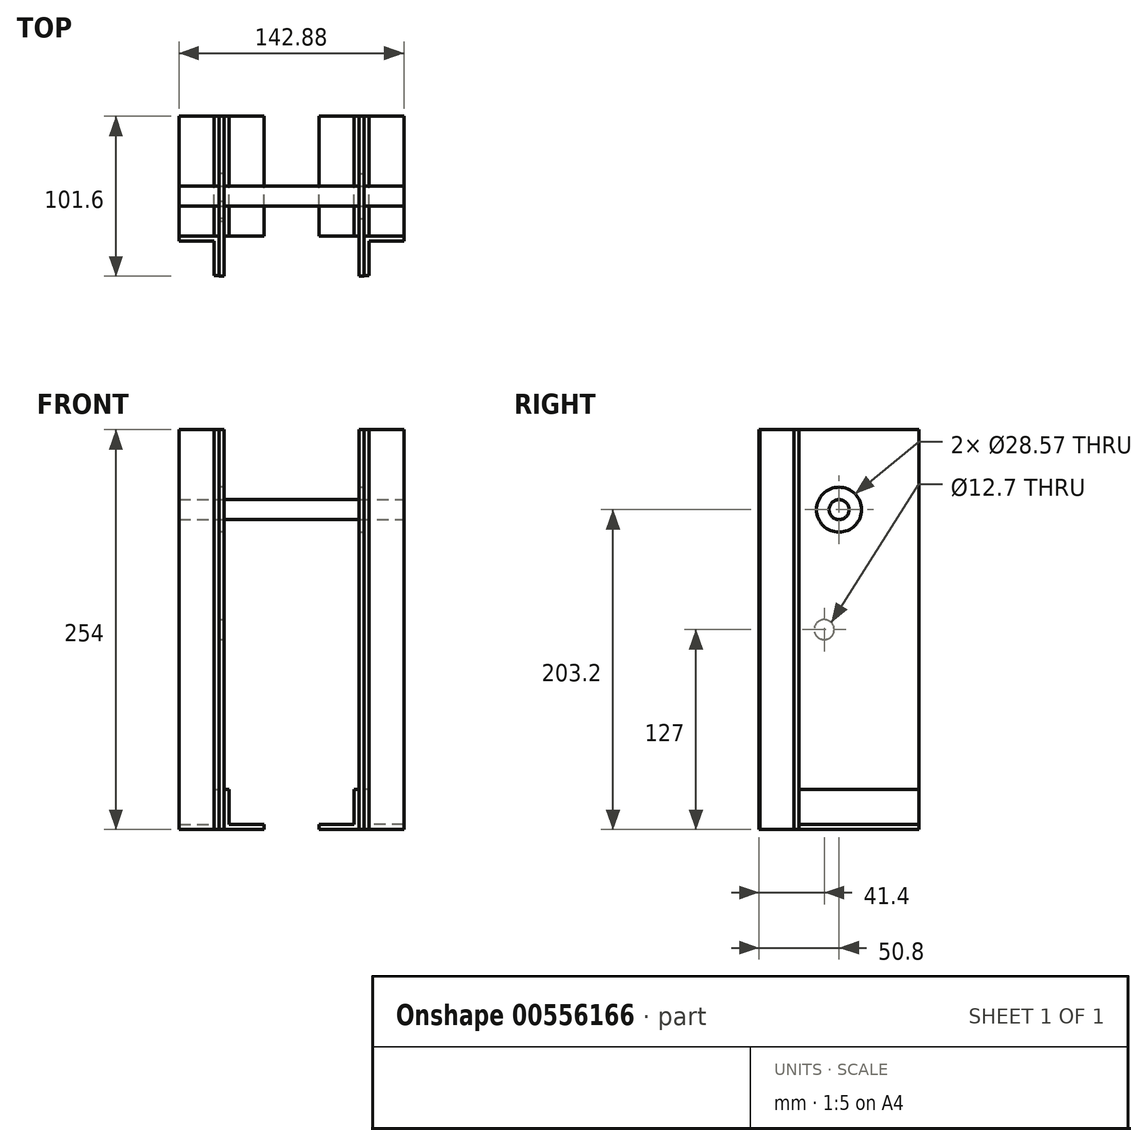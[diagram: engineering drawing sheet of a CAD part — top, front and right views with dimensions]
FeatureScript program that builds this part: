
annotation { "Feature Type Name" : "Feature", "Feature Type Description" : "" }
export const myFeature = defineFeature(function(context is Context, id is Id, definition is map)
    precondition{}
    {
        {
            var Q0;
            Q0=qCreatedBy(makeId("Front.planeOp"),FACE);
            var sketch = newSketch(context, id + "F0", { "sketchPlane" : qUnion([Q0])});
            skLineSegment(sketch, "E0", {"start": v(0, 0) * mm, "end": v(-25.4, 0) * mm});
            skLineSegment(sketch, "E1", {"start": v(-25.4, 0) * mm, "end": v(-25.4, 3.17) * mm});
            skLineSegment(sketch, "E2", {"start": v(-25.4, 3.17) * mm, "end": v(-3.17, 3.17) * mm});
            skLineSegment(sketch, "E3", {"start": v(-3.17, 3.17) * mm, "end": v(-3.18, 25.4) * mm});
            skLineSegment(sketch, "E4", {"start": v(-3.18, 25.4) * mm, "end": v(0, 25.4) * mm});
            skLineSegment(sketch, "E5", {"start": v(0, 25.4) * mm, "end": v(0, 0) * mm});
            skSolve(sketch);
        }
        {
            var Q0;
            Q0 = qSketchRegion(id + "F0", true);
            extrude(context, id + "F1", {"entities" : qUnion([Q0]), "depth" : 76.2 * mm, "offsetDistance" : 25.4 * mm});
        }
        {
            var Q0;
            Q0=qCreatedBy(makeId("Front.planeOp"),FACE);
            var sketch = newSketch(context, id + "F2", { "sketchPlane" : qUnion([Q0])});
            skLineSegment(sketch, "E6.bottom", {"start": v(0, 0) * mm, "end": v(3.18, 0) * mm});
            skLineSegment(sketch, "E6.top", {"start": v(0, 254) * mm, "end": v(3.17, 254) * mm});
            skLineSegment(sketch, "E6.left", {"start": v(0, 0) * mm, "end": v(0, 254) * mm});
            skLineSegment(sketch, "E6.right", {"start": v(3.18, 0) * mm, "end": v(3.17, 254) * mm});
            skSolve(sketch);
        }
        {
            var Q0;
            Q0 = qSketchRegion(id + "F2", true);
            extrude(context, id + "F3", {"entities" : qUnion([Q0]), "depth" : 101.6 * mm, "offsetDistance" : 25.4 * mm});
        }
        {
            var Q0;
            Q0=makeQuery(id+"F3.opExtrude","SWEPT_FACE",FACE,{"disambiguationData":[OSD([sQuery(id+"F2.wireOp",EDGE,"E6.left")])]});
            var sketch = newSketch(context, id + "F4", { "sketchPlane" : qUnion([Q0])});
            skLineSegment(sketch, "E7", {"start": v(0, 254) * mm, "end": v(50.8, 254) * mm, "construction": true});
            skLineSegment(sketch, "E8", {"start": v(50.8, 254) * mm, "end": v(50.8, 203.2) * mm, "construction": true});
            skCircle(sketch, "E9", {"center": v(50.8, 203.2) * mm, "radius": 14.29 * mm});
            skSolve(sketch);
        }
        {
            var Q0;
            Q0 = qSketchRegion(id + "F4", true);
            extrude(context, id + "F5", {"entities" : qUnion([Q0]), "operationType" : NewBodyOperationType.REMOVE, "oppositeDirection" : true, "depth" : 25.4 * mm, "offsetDistance" : 25.4 * mm});
        }
        {
            var Q0;
            Q0=makeQuery(id+"F3.opExtrude","SWEPT_FACE",FACE,{"disambiguationData":[OSD([sQuery(id+"F2.wireOp",EDGE,"E6.left")])]});
            cPlane(context, id + "F6", {"entities" : qUnion([Q0]), "cplaneType" : CPlaneType.OFFSET, "offset" : 1.59 * mm, "oppositeDirection" : true, "width" : 152.4 * mm, "height" : 152.4 * mm});
        }
        {
            var Q0;
            Q0=makeQuery(id+"F1.opExtrude","SWEPT_BODY",BODY,{"disambiguationData":[OSD([sQuery(id+"F0.wireOp",EDGE,"E0"),sQuery(id+"F0.wireOp",EDGE,"E1"),sQuery(id+"F0.wireOp",EDGE,"E2"),sQuery(id+"F0.wireOp",EDGE,"E3"),sQuery(id+"F0.wireOp",EDGE,"E4"),sQuery(id+"F0.wireOp",EDGE,"E5")])]});
            var Q1;
            Q1=qCreatedBy(id+"F6.planeOp",FACE);
            mirror(context, id + "F7", {"entities" : qUnion([Q0]), "mirrorPlane" : qUnion([Q1])});
        }
        {
            var Q0;
            Q0=makeQuery(id+"F1.opExtrude","SWEPT_FACE",FACE,{"disambiguationData":[OSD([sQuery(id+"F0.wireOp",EDGE,"E0")])]});
            var sketch = newSketch(context, id + "F8", { "sketchPlane" : qUnion([Q0])});
            skLineSegment(sketch, "E10", {"start": v(-25.4, 76.2) * mm, "end": v(-25.4, 79.38) * mm});
            skLineSegment(sketch, "E11", {"start": v(-25.4, 79.38) * mm, "end": v(-3.17, 79.38) * mm});
            skLineSegment(sketch, "E12", {"start": v(-3.17, 79.38) * mm, "end": v(-3.18, 101.1) * mm});
            skLineSegment(sketch, "E13", {"start": v(-3.18, 101.1) * mm, "end": v(0, 101.1) * mm});
            skLineSegment(sketch, "E14", {"start": v(0, 101.1) * mm, "end": v(0, 76.2) * mm});
            skLineSegment(sketch, "E15", {"start": v(0, 76.2) * mm, "end": v(-25.4, 76.2) * mm});
            skSolve(sketch);
        }
        {
            var Q0;
            Q0 = qSketchRegion(id + "F8", true);
            extrude(context, id + "F9", {"entities" : qUnion([Q0]), "oppositeDirection" : true, "depth" : 254 * mm, "offsetDistance" : 25.4 * mm});
        }
        {
            var Q0;
            Q0=qCreatedBy(id+"F6.planeOp",FACE);
            cPlane(context, id + "F10", {"entities" : qUnion([Q0]), "cplaneType" : CPlaneType.OFFSET, "offset" : 44.45 * mm, "oppositeDirection" : true, "width" : 152.4 * mm, "height" : 152.4 * mm});
        }
        {
            var Q0;
            Q0=makeQuery(id+"F3.opExtrude","SWEPT_BODY",BODY,{"disambiguationData":[OSD([sQuery(id+"F2.wireOp",EDGE,"E6.bottom"),sQuery(id+"F2.wireOp",EDGE,"E6.top"),sQuery(id+"F2.wireOp",EDGE,"E6.left"),sQuery(id+"F2.wireOp",EDGE,"E6.right")])]});
            var Q1;
            Q1=makeQuery(id+"F7.opPattern","COPY",BODY,{"derivedFrom":makeQuery(id+"F1.opExtrude","SWEPT_BODY",BODY,{"disambiguationData":[OSD([sQuery(id+"F0.wireOp",EDGE,"E0"),sQuery(id+"F0.wireOp",EDGE,"E1"),sQuery(id+"F0.wireOp",EDGE,"E2"),sQuery(id+"F0.wireOp",EDGE,"E3"),sQuery(id+"F0.wireOp",EDGE,"E4"),sQuery(id+"F0.wireOp",EDGE,"E5")])]}),"instanceName":"1"});
            var Q2;
            Q2=makeQuery(id+"F9.opExtrude","SWEPT_BODY",BODY,{"disambiguationData":[OSD([sQuery(id+"F8.wireOp",EDGE,"E10"),sQuery(id+"F8.wireOp",EDGE,"E11"),sQuery(id+"F8.wireOp",EDGE,"E12"),sQuery(id+"F8.wireOp",EDGE,"E13"),sQuery(id+"F8.wireOp",EDGE,"E14"),sQuery(id+"F8.wireOp",EDGE,"E15")])]});
            var Q3;
            Q3=makeQuery(id+"F1.opExtrude","SWEPT_BODY",BODY,{"disambiguationData":[OSD([sQuery(id+"F0.wireOp",EDGE,"E0"),sQuery(id+"F0.wireOp",EDGE,"E1"),sQuery(id+"F0.wireOp",EDGE,"E2"),sQuery(id+"F0.wireOp",EDGE,"E3"),sQuery(id+"F0.wireOp",EDGE,"E4"),sQuery(id+"F0.wireOp",EDGE,"E5")])]});
            var Q4;
            Q4=qCreatedBy(id+"F10.planeOp",FACE);
            mirror(context, id + "F11", {"entities" : qUnion([Q0, Q1, Q2, Q3]), "mirrorPlane" : qUnion([Q4])});
        }
        {
            var Q0;
            Q0=makeQuery(id+"F3.opExtrude","SWEPT_FACE",FACE,{"disambiguationData":[OSD([sQuery(id+"F2.wireOp",EDGE,"E6.left")])]});
            var sketch = newSketch(context, id + "F12", { "sketchPlane" : qUnion([Q0])});
            skCircle(sketch, "E16", {"center": v(50.8, 203.2) * mm, "radius": 6.35 * mm});
            skSolve(sketch);
        }
        {
            var Q0;
            Q0 = qSketchRegion(id + "F12", true);
            var Q1;
            Q1=makeQuery(id+"F9.opExtrude","SWEPT_FACE",FACE,{"disambiguationData":[OSD([sQuery(id+"F8.wireOp",EDGE,"E10")])]});
            var Q2;
            Q2=makeQuery(id+"F11.opPattern","COPY",FACE,{"derivedFrom":makeQuery(id+"F9.opExtrude","SWEPT_FACE",FACE,{"disambiguationData":[OSD([sQuery(id+"F8.wireOp",EDGE,"E10")])]}),"instanceName":"1"});
            extrude(context, id + "F13", {"entities" : qUnion([Q0]), "endBound" : BoundingType.UP_TO_SURFACE, "depth" : 25.4 * mm, "endBoundEntityFace" : qUnion([Q1]), "offsetDistance" : 25.4 * mm, "hasSecondDirection" : true, "secondDirectionBound" : SecondDirectionBoundingType.UP_TO_SURFACE, "secondDirectionOppositeDirection" : true, "secondDirectionDepth" : 127 * mm, "secondDirectionBoundEntityFace" : qUnion([Q2])});
        }
        {
            var Q0;
            Q0=makeQuery(id+"F3.opExtrude","SWEPT_FACE",FACE,{"disambiguationData":[OSD([sQuery(id+"F2.wireOp",EDGE,"E6.right")])]});
            var sketch = newSketch(context, id + "F14", { "sketchPlane" : qUnion([Q0])});
            skCircle(sketch, "E17", {"center": v(-60.2, 127) * mm, "radius": 6.35 * mm});
            skLineSegment(sketch, "E18", {"start": v(-50.8, 203.2) * mm, "end": v(-101.6, 203.2) * mm, "construction": true});
            skSolve(sketch);
        }
        {
            var Q0;
            Q0=makeQuery(id+"F14.imprint","IMPRINT",FACE,{"disambiguationData":[TD([[makeQuery(id+"F14.imprint","IMPRINT",EDGE,{"derivedFrom":sQuery(id+"F14.wireOp",EDGE,"E17")}),1.0]])]});
            extrude(context, id + "F15", {"entities" : qUnion([Q0]), "operationType" : NewBodyOperationType.REMOVE, "oppositeDirection" : true, "depth" : 25.4 * mm, "offsetDistance" : 25.4 * mm});
        }
    });
